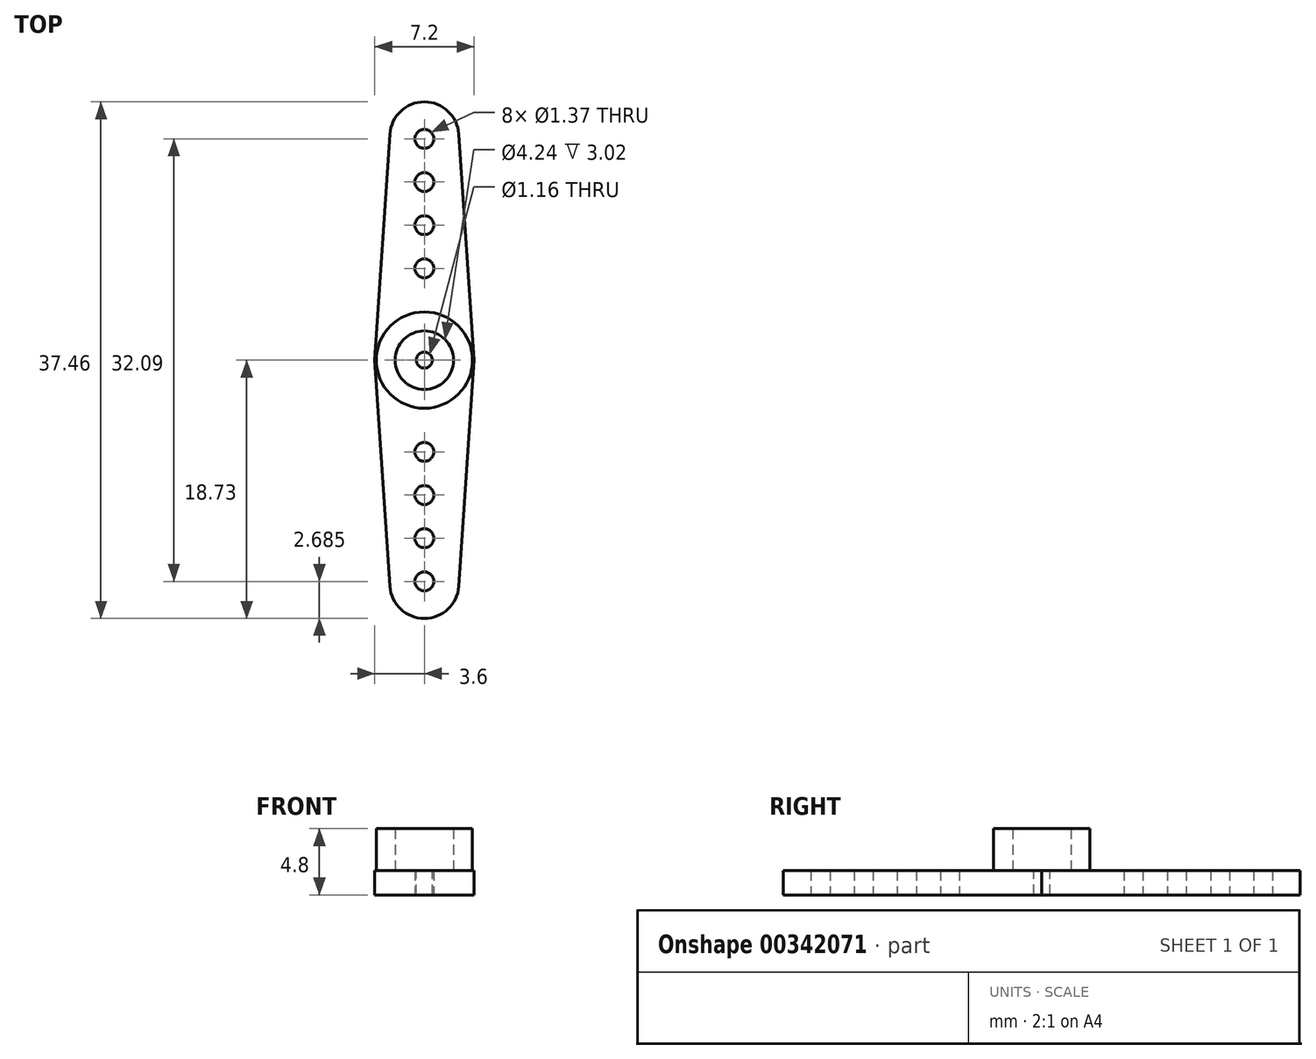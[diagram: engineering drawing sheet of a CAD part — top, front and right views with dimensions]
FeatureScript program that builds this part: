
annotation { "Feature Type Name" : "Feature", "Feature Type Description" : "" }
export const myFeature = defineFeature(function(context is Context, id is Id, definition is map)
    precondition{}
    {
        {
            var Q0;
            Q0=qCreatedBy(makeId("Top.planeOp"),FACE);
            var sketch = newSketch(context, id + "F0", { "sketchPlane" : qUnion([Q0])});
            skArc(sketch, "E0", {"start": v(-3.57, 0.48) * mm, "mid": v(0, -3.6) * mm, "end": v(3.57, 0.48) * mm, "construction": true});
            skArc(sketch, "E1", {"start": v(2.5, 16.4) * mm, "mid": v(0, 18.73) * mm, "end": v(-2.5, 16.4) * mm});
            skPoint(sketch, "E2", {"position": v(0, 18.73) * mm});
            skLineSegment(sketch, "E3", {"start": v(-3.6, 0) * mm, "end": v(-2.5, 16.4) * mm});
            skLineSegment(sketch, "E4", {"start": v(3.6, 0) * mm, "end": v(2.5, 16.4) * mm});
            skCircle(sketch, "E5", {"center": v(0, 16.05) * mm, "radius": 0.69 * mm});
            skCircle(sketch, "E6.0.1.0", {"center": v(0, 12.92) * mm, "radius": 0.69 * mm});
            skCircle(sketch, "E6.0.2.0", {"center": v(0, 9.79) * mm, "radius": 0.69 * mm});
            skCircle(sketch, "E6.0.3.0", {"center": v(0, 6.66) * mm, "radius": 0.69 * mm});
            skLineSegment(sketch, "E6.direction1", {"start": v(0, 16.05) * mm, "end": v(25, 16.05) * mm, "construction": true});
            skLineSegment(sketch, "E6.direction2", {"start": v(0, 16.05) * mm, "end": v(0, 12.92) * mm, "construction": true});
            skLineSegment(sketch, "E7", {"start": v(-16.15, 0) * mm, "end": v(19.67, 0) * mm, "construction": true});
            skCircle(sketch, "E8.MirrorC", {"center": v(0, -16.05) * mm, "radius": 0.69 * mm});
            skArc(sketch, "E9.MirrorCS", {"start": v(2.5, -16.4) * mm, "mid": v(0, -18.73) * mm, "end": v(-2.5, -16.4) * mm});
            skLineSegment(sketch, "E10.MirrorCS", {"start": v(0, -16.05) * mm, "end": v(0, -12.92) * mm, "construction": true});
            skCircle(sketch, "E11.MirrorC", {"center": v(0, -12.92) * mm, "radius": 0.69 * mm});
            skPoint(sketch, "E12.MirrorP", {"position": v(0, -18.73) * mm});
            skCircle(sketch, "E13.MirrorC", {"center": v(0, -9.79) * mm, "radius": 0.69 * mm});
            skCircle(sketch, "E14.MirrorC", {"center": v(0, -6.66) * mm, "radius": 0.69 * mm});
            skLineSegment(sketch, "E15.MirrorCS", {"start": v(0, -16.05) * mm, "end": v(25, -16.05) * mm, "construction": true});
            skLineSegment(sketch, "E16.MirrorCS", {"start": v(3.6, 0) * mm, "end": v(2.5, -16.4) * mm});
            skLineSegment(sketch, "E17.MirrorCS", {"start": v(-3.6, 0) * mm, "end": v(-2.5, -16.4) * mm});
            skSolve(sketch);
        }
        {
            var Q0;
            Q0 = qSketchRegion(id + "F0", true);
            extrude(context, id + "F1", {"entities" : qUnion([Q0]), "depth" : 1.78 * mm});
        }
        {
            var Q0;
            Q0=makeQuery(id+"F1.opExtrude","CAP_FACE",FACE,{"disambiguationData":[OSD([sQuery(id+"F0.wireOp",EDGE,"E1"),sQuery(id+"F0.wireOp",EDGE,"E3"),sQuery(id+"F0.wireOp",EDGE,"E4"),sQuery(id+"F0.wireOp",EDGE,"E5"),sQuery(id+"F0.wireOp",EDGE,"E6.0.1.0"),sQuery(id+"F0.wireOp",EDGE,"E6.0.2.0"),sQuery(id+"F0.wireOp",EDGE,"E6.0.3.0"),sQuery(id+"F0.wireOp",EDGE,"E8.MirrorC"),sQuery(id+"F0.wireOp",EDGE,"E9.MirrorCS"),sQuery(id+"F0.wireOp",EDGE,"E11.MirrorC"),sQuery(id+"F0.wireOp",EDGE,"E13.MirrorC"),sQuery(id+"F0.wireOp",EDGE,"E14.MirrorC"),sQuery(id+"F0.wireOp",EDGE,"E16.MirrorCS"),sQuery(id+"F0.wireOp",EDGE,"E17.MirrorCS")])],"isStart":false});
            var sketch = newSketch(context, id + "F2", { "sketchPlane" : qUnion([Q0])});
            skCircle(sketch, "E18", {"center": v(0, 0) * mm, "radius": 3.5 * mm});
            skCircle(sketch, "E19.0", {"center": v(0, 0) * mm, "radius": 2.12 * mm});
            skSolve(sketch);
        }
        {
            var Q0;
            Q0 = qSketchRegion(id + "F2", true);
            var Q1;
            Q1 = qConstructionFilter(qBodyType(qCreatedBy(id + "F2" ,EDGE), BodyType.WIRE), ConstructionObject.NO);
            extrude(context, id + "F3", {"entities" : qUnion([Q0]), "operationType" : NewBodyOperationType.ADD, "surfaceEntities" : qUnion([Q1]), "depth" : 3.02 * mm});
        }
        {
            var Q0;
            Q0=makeQuery(id+"F3.boolean.opBoolean","SPLIT",FACE,{"disambiguationData":[TD([makeQuery(id+"F3.opExtrude","SWEPT_FACE",FACE,{"disambiguationData":[OSD([sQuery(id+"F2.wireOp",EDGE,"E19.0")])]})])],"derivedFrom":makeQuery(id+"F1.opExtrude","CAP_FACE",FACE,{"disambiguationData":[OSD([sQuery(id+"F0.wireOp",EDGE,"E1"),sQuery(id+"F0.wireOp",EDGE,"E3"),sQuery(id+"F0.wireOp",EDGE,"E4"),sQuery(id+"F0.wireOp",EDGE,"E5"),sQuery(id+"F0.wireOp",EDGE,"E6.0.1.0"),sQuery(id+"F0.wireOp",EDGE,"E6.0.2.0"),sQuery(id+"F0.wireOp",EDGE,"E6.0.3.0"),sQuery(id+"F0.wireOp",EDGE,"E8.MirrorC"),sQuery(id+"F0.wireOp",EDGE,"E9.MirrorCS"),sQuery(id+"F0.wireOp",EDGE,"E11.MirrorC"),sQuery(id+"F0.wireOp",EDGE,"E13.MirrorC"),sQuery(id+"F0.wireOp",EDGE,"E14.MirrorC"),sQuery(id+"F0.wireOp",EDGE,"E16.MirrorCS"),sQuery(id+"F0.wireOp",EDGE,"E17.MirrorCS")])],"isStart":false})});
            var sketch = newSketch(context, id + "F4", { "sketchPlane" : qUnion([Q0])});
            skCircle(sketch, "E20", {"center": v(0, 0) * mm, "radius": 0.58 * mm});
            skSolve(sketch);
        }
        {
            var Q0;
            Q0 = qSketchRegion(id + "F4", true);
            extrude(context, id + "F5", {"entities" : qUnion([Q0]), "operationType" : NewBodyOperationType.REMOVE, "endBound" : BoundingType.UP_TO_NEXT, "oppositeDirection" : true, "depth" : 25 * mm});
        }
    });
